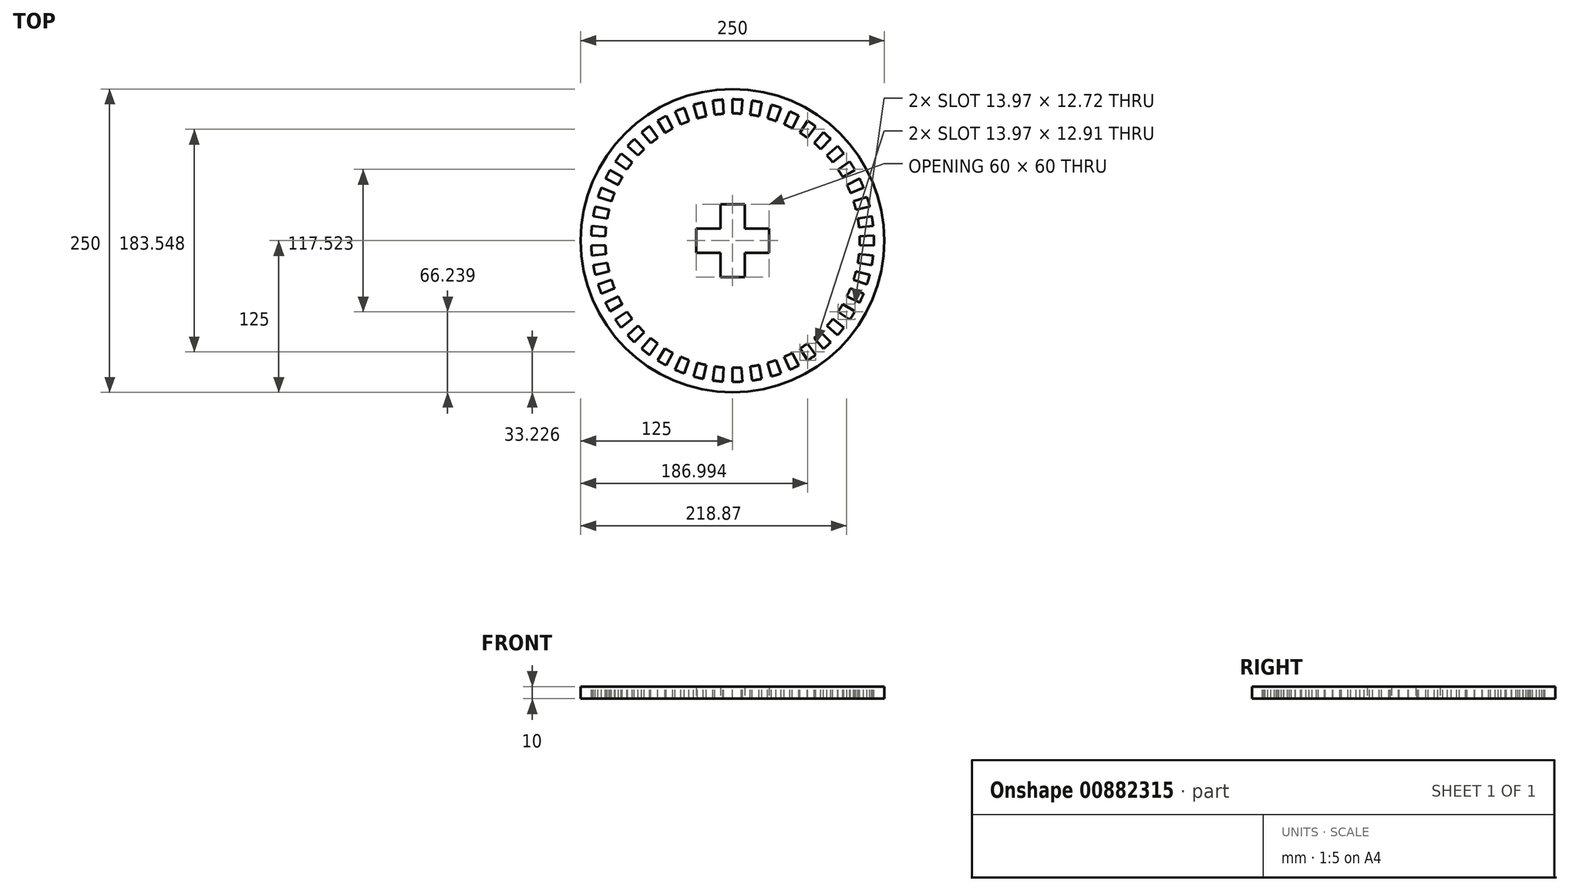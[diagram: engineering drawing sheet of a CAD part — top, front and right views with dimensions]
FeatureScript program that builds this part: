
annotation { "Feature Type Name" : "Feature", "Feature Type Description" : "" }
export const myFeature = defineFeature(function(context is Context, id is Id, definition is map)
    precondition{}
    {
        {
            var Q0;
            Q0=qCreatedBy(makeId("Top.planeOp"),FACE);
            var sketch = newSketch(context, id + "F0", { "sketchPlane" : qUnion([Q0])});
            skCircle(sketch, "E0", {"center": v(0, 0) * mm, "radius": 145 * mm});
            skArc(sketch, "E1", {"start": v(9.54, 136.41) * mm, "mid": v(4.77, 136.66) * mm, "end": v(0, 136.75) * mm});
            skArc(sketch, "E2", {"start": v(8, 114.55) * mm, "mid": v(4, 114.76) * mm, "end": v(0, 114.83) * mm});
            skLineSegment(sketch, "E3", {"start": v(0, 0) * mm, "end": v(0, 38.61) * mm, "construction": true});
            skLineSegment(sketch, "E4", {"start": v(0, 38.61) * mm, "end": v(0, 0) * mm, "construction": true});
            skLineSegment(sketch, "E5", {"start": v(0, 0) * mm, "end": v(-47.77, 0) * mm, "construction": true});
            skLineSegment(sketch, "E6", {"start": v(0, 30) * mm, "end": v(-10, 30) * mm});
            skLineSegment(sketch, "E7", {"start": v(-10, 30) * mm, "end": v(-10, 10) * mm});
            skLineSegment(sketch, "E8", {"start": v(-10, 10) * mm, "end": v(-30, 10) * mm});
            skLineSegment(sketch, "E9", {"start": v(-30, 10) * mm, "end": v(-30, 0) * mm});
            skLineSegment(sketch, "E10.MirrorCS", {"start": v(-30, -10) * mm, "end": v(-30, 0) * mm});
            skLineSegment(sketch, "E11.MirrorCS", {"start": v(-10, -10) * mm, "end": v(-30, -10) * mm});
            skLineSegment(sketch, "E12.MirrorCS", {"start": v(-10, -30) * mm, "end": v(-10, -10) * mm});
            skLineSegment(sketch, "E13.MirrorCS", {"start": v(0, -30) * mm, "end": v(-10, -30) * mm});
            skLineSegment(sketch, "E14.MirrorCS", {"start": v(0, 30) * mm, "end": v(10, 30) * mm});
            skLineSegment(sketch, "E15.MirrorCS", {"start": v(10, 30) * mm, "end": v(10, 10) * mm});
            skLineSegment(sketch, "E16.MirrorCS", {"start": v(10, 10) * mm, "end": v(30, 10) * mm});
            skLineSegment(sketch, "E17.MirrorCS", {"start": v(30, 10) * mm, "end": v(30, 0) * mm});
            skLineSegment(sketch, "E18.MirrorCS", {"start": v(30, -10) * mm, "end": v(30, 0) * mm});
            skLineSegment(sketch, "E19.MirrorCS", {"start": v(10, -10) * mm, "end": v(30, -10) * mm});
            skLineSegment(sketch, "E20.MirrorCS", {"start": v(0, -30) * mm, "end": v(10, -30) * mm});
            skLineSegment(sketch, "E21.MirrorCS", {"start": v(10, -30) * mm, "end": v(10, -10) * mm});
            skLineSegment(sketch, "E22", {"start": v(0, 114.83) * mm, "end": v(0, 136.75) * mm});
            skLineSegment(sketch, "E23", {"start": v(8, 114.55) * mm, "end": v(9.54, 136.41) * mm});
            skArc(sketch, "E24.1.0", {"start": v(-10, 114.4) * mm, "mid": v(-14, 113.98) * mm, "end": v(-17.96, 113.42) * mm});
            skLineSegment(sketch, "E24.1.1", {"start": v(-17.96, 113.42) * mm, "end": v(-21.4, 135.06) * mm});
            skArc(sketch, "E24.1.2", {"start": v(-11.92, 136.23) * mm, "mid": v(-16.67, 135.73) * mm, "end": v(-21.4, 135.06) * mm});
            skLineSegment(sketch, "E24.1.3", {"start": v(-10, 114.4) * mm, "end": v(-11.92, 136.23) * mm});
            skArc(sketch, "E24.2.0", {"start": v(-27.78, 111.42) * mm, "mid": v(-31.65, 110.39) * mm, "end": v(-35.49, 109.21) * mm});
            skLineSegment(sketch, "E24.2.1", {"start": v(-35.49, 109.21) * mm, "end": v(-42.26, 130.05) * mm});
            skArc(sketch, "E24.2.2", {"start": v(-33.08, 132.68) * mm, "mid": v(-37.7, 131.45) * mm, "end": v(-42.26, 130.05) * mm});
            skLineSegment(sketch, "E24.2.3", {"start": v(-27.78, 111.42) * mm, "end": v(-33.08, 132.68) * mm});
            skArc(sketch, "E24.3.0", {"start": v(-44.87, 105.7) * mm, "mid": v(-48.53, 104.07) * mm, "end": v(-52.13, 102.32) * mm});
            skLineSegment(sketch, "E24.3.1", {"start": v(-52.13, 102.32) * mm, "end": v(-62.08, 121.84) * mm});
            skArc(sketch, "E24.3.2", {"start": v(-53.43, 125.88) * mm, "mid": v(-57.8, 123.93) * mm, "end": v(-62.08, 121.84) * mm});
            skLineSegment(sketch, "E24.3.3", {"start": v(-44.87, 105.7) * mm, "end": v(-53.43, 125.88) * mm});
            skArc(sketch, "E24.4.0", {"start": v(-60.85, 97.38) * mm, "mid": v(-64.21, 95.2) * mm, "end": v(-67.5, 92.9) * mm});
            skLineSegment(sketch, "E24.4.1", {"start": v(-67.5, 92.9) * mm, "end": v(-80.38, 110.63) * mm});
            skArc(sketch, "E24.4.2", {"start": v(-72.47, 115.97) * mm, "mid": v(-76.47, 113.37) * mm, "end": v(-80.38, 110.63) * mm});
            skLineSegment(sketch, "E24.4.3", {"start": v(-60.85, 97.38) * mm, "end": v(-72.47, 115.97) * mm});
            skArc(sketch, "E24.5.0", {"start": v(-75.34, 86.67) * mm, "mid": v(-78.32, 83.98) * mm, "end": v(-81.2, 81.2) * mm});
            skLineSegment(sketch, "E24.5.1", {"start": v(-81.2, 81.2) * mm, "end": v(-96.7, 96.7) * mm});
            skArc(sketch, "E24.5.2", {"start": v(-89.71, 103.2) * mm, "mid": v(-93.26, 100.01) * mm, "end": v(-96.7, 96.7) * mm});
            skLineSegment(sketch, "E24.5.3", {"start": v(-75.34, 86.67) * mm, "end": v(-89.71, 103.2) * mm});
            skArc(sketch, "E24.6.0", {"start": v(-87.97, 73.81) * mm, "mid": v(-90.5, 70.7) * mm, "end": v(-92.9, 67.5) * mm});
            skLineSegment(sketch, "E24.6.1", {"start": v(-92.9, 67.5) * mm, "end": v(-110.63, 80.38) * mm});
            skArc(sketch, "E24.6.2", {"start": v(-104.75, 87.9) * mm, "mid": v(-107.76, 84.19) * mm, "end": v(-110.63, 80.38) * mm});
            skLineSegment(sketch, "E24.6.3", {"start": v(-87.97, 73.81) * mm, "end": v(-104.75, 87.9) * mm});
            skArc(sketch, "E24.7.0", {"start": v(-98.43, 59.14) * mm, "mid": v(-100.44, 55.67) * mm, "end": v(-102.32, 52.13) * mm});
            skLineSegment(sketch, "E24.7.1", {"start": v(-102.32, 52.13) * mm, "end": v(-121.84, 62.08) * mm});
            skArc(sketch, "E24.7.2", {"start": v(-117.22, 70.43) * mm, "mid": v(-119.6, 66.3) * mm, "end": v(-121.84, 62.08) * mm});
            skLineSegment(sketch, "E24.7.3", {"start": v(-98.43, 59.14) * mm, "end": v(-117.22, 70.43) * mm});
            skArc(sketch, "E24.8.0", {"start": v(-106.47, 43.02) * mm, "mid": v(-107.9, 39.28) * mm, "end": v(-109.21, 35.49) * mm});
            skLineSegment(sketch, "E24.8.1", {"start": v(-109.21, 35.49) * mm, "end": v(-130.05, 42.26) * mm});
            skArc(sketch, "E24.8.2", {"start": v(-126.79, 51.23) * mm, "mid": v(-128.5, 46.77) * mm, "end": v(-130.05, 42.26) * mm});
            skLineSegment(sketch, "E24.8.3", {"start": v(-106.47, 43.02) * mm, "end": v(-126.79, 51.23) * mm});
            skArc(sketch, "E24.9.0", {"start": v(-111.9, 25.83) * mm, "mid": v(-112.72, 21.91) * mm, "end": v(-113.42, 17.96) * mm});
            skLineSegment(sketch, "E24.9.1", {"start": v(-113.42, 17.96) * mm, "end": v(-135.06, 21.4) * mm});
            skArc(sketch, "E24.9.2", {"start": v(-133.24, 30.76) * mm, "mid": v(-134.23, 26.1) * mm, "end": v(-135.06, 21.4) * mm});
            skLineSegment(sketch, "E24.9.3", {"start": v(-111.9, 25.83) * mm, "end": v(-133.24, 30.76) * mm});
            skArc(sketch, "E24.10.0", {"start": v(-114.55, 8) * mm, "mid": v(-114.76, 4) * mm, "end": v(-114.83, 0) * mm});
            skLineSegment(sketch, "E24.10.1", {"start": v(-114.83, 0) * mm, "end": v(-136.75, 0) * mm});
            skArc(sketch, "E24.10.2", {"start": v(-136.41, 9.54) * mm, "mid": v(-136.66, 4.77) * mm, "end": v(-136.75, 0) * mm});
            skLineSegment(sketch, "E24.10.3", {"start": v(-114.55, 8) * mm, "end": v(-136.41, 9.54) * mm});
            skArc(sketch, "E24.11.0", {"start": v(-114.4, -10) * mm, "mid": v(-113.98, -14) * mm, "end": v(-113.42, -17.96) * mm});
            skLineSegment(sketch, "E24.11.1", {"start": v(-113.42, -17.96) * mm, "end": v(-135.06, -21.4) * mm});
            skArc(sketch, "E24.11.2", {"start": v(-136.23, -11.92) * mm, "mid": v(-135.73, -16.67) * mm, "end": v(-135.06, -21.4) * mm});
            skLineSegment(sketch, "E24.11.3", {"start": v(-114.4, -10) * mm, "end": v(-136.23, -11.92) * mm});
            skArc(sketch, "E24.12.0", {"start": v(-111.42, -27.78) * mm, "mid": v(-110.39, -31.65) * mm, "end": v(-109.21, -35.49) * mm});
            skLineSegment(sketch, "E24.12.1", {"start": v(-109.21, -35.49) * mm, "end": v(-130.05, -42.26) * mm});
            skArc(sketch, "E24.12.2", {"start": v(-132.68, -33.08) * mm, "mid": v(-131.45, -37.7) * mm, "end": v(-130.05, -42.26) * mm});
            skLineSegment(sketch, "E24.12.3", {"start": v(-111.42, -27.78) * mm, "end": v(-132.68, -33.08) * mm});
            skArc(sketch, "E24.13.0", {"start": v(-105.7, -44.87) * mm, "mid": v(-104.07, -48.53) * mm, "end": v(-102.32, -52.13) * mm});
            skLineSegment(sketch, "E24.13.1", {"start": v(-102.32, -52.13) * mm, "end": v(-121.84, -62.08) * mm});
            skArc(sketch, "E24.13.2", {"start": v(-125.88, -53.43) * mm, "mid": v(-123.93, -57.8) * mm, "end": v(-121.84, -62.08) * mm});
            skLineSegment(sketch, "E24.13.3", {"start": v(-105.7, -44.87) * mm, "end": v(-125.88, -53.43) * mm});
            skArc(sketch, "E24.14.0", {"start": v(-97.38, -60.85) * mm, "mid": v(-95.2, -64.21) * mm, "end": v(-92.9, -67.5) * mm});
            skLineSegment(sketch, "E24.14.1", {"start": v(-92.9, -67.5) * mm, "end": v(-110.63, -80.38) * mm});
            skArc(sketch, "E24.14.2", {"start": v(-115.97, -72.47) * mm, "mid": v(-113.37, -76.47) * mm, "end": v(-110.63, -80.38) * mm});
            skLineSegment(sketch, "E24.14.3", {"start": v(-97.38, -60.85) * mm, "end": v(-115.97, -72.47) * mm});
            skArc(sketch, "E24.15.0", {"start": v(-86.67, -75.34) * mm, "mid": v(-83.98, -78.32) * mm, "end": v(-81.2, -81.2) * mm});
            skLineSegment(sketch, "E24.15.1", {"start": v(-81.2, -81.2) * mm, "end": v(-96.7, -96.7) * mm});
            skArc(sketch, "E24.15.2", {"start": v(-103.2, -89.71) * mm, "mid": v(-100.01, -93.26) * mm, "end": v(-96.7, -96.7) * mm});
            skLineSegment(sketch, "E24.15.3", {"start": v(-86.67, -75.34) * mm, "end": v(-103.2, -89.71) * mm});
            skArc(sketch, "E24.16.0", {"start": v(-73.81, -87.97) * mm, "mid": v(-70.7, -90.5) * mm, "end": v(-67.5, -92.9) * mm});
            skLineSegment(sketch, "E24.16.1", {"start": v(-67.5, -92.9) * mm, "end": v(-80.38, -110.63) * mm});
            skArc(sketch, "E24.16.2", {"start": v(-87.9, -104.75) * mm, "mid": v(-84.19, -107.76) * mm, "end": v(-80.38, -110.63) * mm});
            skLineSegment(sketch, "E24.16.3", {"start": v(-73.81, -87.97) * mm, "end": v(-87.9, -104.75) * mm});
            skArc(sketch, "E24.17.0", {"start": v(-59.14, -98.43) * mm, "mid": v(-55.67, -100.44) * mm, "end": v(-52.13, -102.32) * mm});
            skLineSegment(sketch, "E24.17.1", {"start": v(-52.13, -102.32) * mm, "end": v(-62.08, -121.84) * mm});
            skArc(sketch, "E24.17.2", {"start": v(-70.43, -117.22) * mm, "mid": v(-66.3, -119.6) * mm, "end": v(-62.08, -121.84) * mm});
            skLineSegment(sketch, "E24.17.3", {"start": v(-59.14, -98.43) * mm, "end": v(-70.43, -117.22) * mm});
            skArc(sketch, "E24.18.0", {"start": v(-43.02, -106.47) * mm, "mid": v(-39.28, -107.9) * mm, "end": v(-35.49, -109.21) * mm});
            skLineSegment(sketch, "E24.18.1", {"start": v(-35.49, -109.21) * mm, "end": v(-42.26, -130.05) * mm});
            skArc(sketch, "E24.18.2", {"start": v(-51.23, -126.79) * mm, "mid": v(-46.77, -128.5) * mm, "end": v(-42.26, -130.05) * mm});
            skLineSegment(sketch, "E24.18.3", {"start": v(-43.02, -106.47) * mm, "end": v(-51.23, -126.79) * mm});
            skArc(sketch, "E24.19.0", {"start": v(-25.83, -111.9) * mm, "mid": v(-21.91, -112.72) * mm, "end": v(-17.96, -113.42) * mm});
            skLineSegment(sketch, "E24.19.1", {"start": v(-17.96, -113.42) * mm, "end": v(-21.4, -135.06) * mm});
            skArc(sketch, "E24.19.2", {"start": v(-30.76, -133.24) * mm, "mid": v(-26.1, -134.23) * mm, "end": v(-21.4, -135.06) * mm});
            skLineSegment(sketch, "E24.19.3", {"start": v(-25.83, -111.9) * mm, "end": v(-30.76, -133.24) * mm});
            skArc(sketch, "E24.20.0", {"start": v(-8, -114.55) * mm, "mid": v(-4, -114.76) * mm, "end": v(0, -114.83) * mm});
            skLineSegment(sketch, "E24.20.1", {"start": v(0, -114.83) * mm, "end": v(0, -136.75) * mm});
            skArc(sketch, "E24.20.2", {"start": v(-9.54, -136.41) * mm, "mid": v(-4.77, -136.66) * mm, "end": v(0, -136.75) * mm});
            skLineSegment(sketch, "E24.20.3", {"start": v(-8, -114.55) * mm, "end": v(-9.54, -136.41) * mm});
            skArc(sketch, "E24.21.0", {"start": v(10, -114.4) * mm, "mid": v(14, -113.98) * mm, "end": v(17.96, -113.42) * mm});
            skLineSegment(sketch, "E24.21.1", {"start": v(17.96, -113.42) * mm, "end": v(21.4, -135.06) * mm});
            skArc(sketch, "E24.21.2", {"start": v(11.92, -136.23) * mm, "mid": v(16.67, -135.73) * mm, "end": v(21.4, -135.06) * mm});
            skLineSegment(sketch, "E24.21.3", {"start": v(10, -114.4) * mm, "end": v(11.92, -136.23) * mm});
            skArc(sketch, "E24.22.0", {"start": v(27.78, -111.42) * mm, "mid": v(31.65, -110.39) * mm, "end": v(35.49, -109.21) * mm});
            skLineSegment(sketch, "E24.22.1", {"start": v(35.49, -109.21) * mm, "end": v(42.26, -130.05) * mm});
            skArc(sketch, "E24.22.2", {"start": v(33.08, -132.68) * mm, "mid": v(37.7, -131.45) * mm, "end": v(42.26, -130.05) * mm});
            skLineSegment(sketch, "E24.22.3", {"start": v(27.78, -111.42) * mm, "end": v(33.08, -132.68) * mm});
            skArc(sketch, "E24.23.0", {"start": v(44.87, -105.7) * mm, "mid": v(48.53, -104.07) * mm, "end": v(52.13, -102.32) * mm});
            skLineSegment(sketch, "E24.23.1", {"start": v(52.13, -102.32) * mm, "end": v(62.08, -121.84) * mm});
            skArc(sketch, "E24.23.2", {"start": v(53.43, -125.88) * mm, "mid": v(57.8, -123.93) * mm, "end": v(62.08, -121.84) * mm});
            skLineSegment(sketch, "E24.23.3", {"start": v(44.87, -105.7) * mm, "end": v(53.43, -125.88) * mm});
            skArc(sketch, "E24.24.0", {"start": v(60.85, -97.38) * mm, "mid": v(64.21, -95.2) * mm, "end": v(67.5, -92.9) * mm});
            skLineSegment(sketch, "E24.24.1", {"start": v(67.5, -92.9) * mm, "end": v(80.38, -110.63) * mm});
            skArc(sketch, "E24.24.2", {"start": v(72.47, -115.97) * mm, "mid": v(76.47, -113.37) * mm, "end": v(80.38, -110.63) * mm});
            skLineSegment(sketch, "E24.24.3", {"start": v(60.85, -97.38) * mm, "end": v(72.47, -115.97) * mm});
            skArc(sketch, "E24.25.0", {"start": v(75.34, -86.67) * mm, "mid": v(78.32, -83.98) * mm, "end": v(81.2, -81.2) * mm});
            skLineSegment(sketch, "E24.25.1", {"start": v(81.2, -81.2) * mm, "end": v(96.7, -96.7) * mm});
            skArc(sketch, "E24.25.2", {"start": v(89.71, -103.2) * mm, "mid": v(93.26, -100.01) * mm, "end": v(96.7, -96.7) * mm});
            skLineSegment(sketch, "E24.25.3", {"start": v(75.34, -86.67) * mm, "end": v(89.71, -103.2) * mm});
            skArc(sketch, "E24.26.0", {"start": v(87.97, -73.81) * mm, "mid": v(90.5, -70.7) * mm, "end": v(92.9, -67.5) * mm});
            skLineSegment(sketch, "E24.26.1", {"start": v(92.9, -67.5) * mm, "end": v(110.63, -80.38) * mm});
            skArc(sketch, "E24.26.2", {"start": v(104.75, -87.9) * mm, "mid": v(107.76, -84.19) * mm, "end": v(110.63, -80.38) * mm});
            skLineSegment(sketch, "E24.26.3", {"start": v(87.97, -73.81) * mm, "end": v(104.75, -87.9) * mm});
            skArc(sketch, "E24.27.0", {"start": v(98.43, -59.14) * mm, "mid": v(100.44, -55.67) * mm, "end": v(102.32, -52.13) * mm});
            skLineSegment(sketch, "E24.27.1", {"start": v(102.32, -52.13) * mm, "end": v(121.84, -62.08) * mm});
            skArc(sketch, "E24.27.2", {"start": v(117.22, -70.43) * mm, "mid": v(119.6, -66.3) * mm, "end": v(121.84, -62.08) * mm});
            skLineSegment(sketch, "E24.27.3", {"start": v(98.43, -59.14) * mm, "end": v(117.22, -70.43) * mm});
            skArc(sketch, "E24.28.0", {"start": v(106.47, -43.02) * mm, "mid": v(107.9, -39.28) * mm, "end": v(109.21, -35.49) * mm});
            skLineSegment(sketch, "E24.28.1", {"start": v(109.21, -35.49) * mm, "end": v(130.05, -42.26) * mm});
            skArc(sketch, "E24.28.2", {"start": v(126.79, -51.23) * mm, "mid": v(128.5, -46.77) * mm, "end": v(130.05, -42.26) * mm});
            skLineSegment(sketch, "E24.28.3", {"start": v(106.47, -43.02) * mm, "end": v(126.79, -51.23) * mm});
            skArc(sketch, "E24.29.0", {"start": v(111.9, -25.83) * mm, "mid": v(112.72, -21.91) * mm, "end": v(113.42, -17.96) * mm});
            skLineSegment(sketch, "E24.29.1", {"start": v(113.42, -17.96) * mm, "end": v(135.06, -21.4) * mm});
            skArc(sketch, "E24.29.2", {"start": v(133.24, -30.76) * mm, "mid": v(134.23, -26.1) * mm, "end": v(135.06, -21.4) * mm});
            skLineSegment(sketch, "E24.29.3", {"start": v(111.9, -25.83) * mm, "end": v(133.24, -30.76) * mm});
            skArc(sketch, "E24.30.0", {"start": v(114.55, -8) * mm, "mid": v(114.76, -4) * mm, "end": v(114.83, 0) * mm});
            skLineSegment(sketch, "E24.30.1", {"start": v(114.83, 0) * mm, "end": v(136.75, 0) * mm});
            skArc(sketch, "E24.30.2", {"start": v(136.41, -9.54) * mm, "mid": v(136.66, -4.77) * mm, "end": v(136.75, 0) * mm});
            skLineSegment(sketch, "E24.30.3", {"start": v(114.55, -8) * mm, "end": v(136.41, -9.54) * mm});
            skArc(sketch, "E24.31.0", {"start": v(114.4, 10) * mm, "mid": v(113.98, 14) * mm, "end": v(113.42, 17.96) * mm});
            skLineSegment(sketch, "E24.31.1", {"start": v(113.42, 17.96) * mm, "end": v(135.06, 21.4) * mm});
            skArc(sketch, "E24.31.2", {"start": v(136.23, 11.92) * mm, "mid": v(135.73, 16.67) * mm, "end": v(135.06, 21.4) * mm});
            skLineSegment(sketch, "E24.31.3", {"start": v(114.4, 10) * mm, "end": v(136.23, 11.92) * mm});
            skArc(sketch, "E24.32.0", {"start": v(111.42, 27.78) * mm, "mid": v(110.39, 31.65) * mm, "end": v(109.21, 35.49) * mm});
            skLineSegment(sketch, "E24.32.1", {"start": v(109.21, 35.49) * mm, "end": v(130.05, 42.26) * mm});
            skArc(sketch, "E24.32.2", {"start": v(132.68, 33.08) * mm, "mid": v(131.45, 37.7) * mm, "end": v(130.05, 42.26) * mm});
            skLineSegment(sketch, "E24.32.3", {"start": v(111.42, 27.78) * mm, "end": v(132.68, 33.08) * mm});
            skArc(sketch, "E24.33.0", {"start": v(105.7, 44.87) * mm, "mid": v(104.07, 48.53) * mm, "end": v(102.32, 52.13) * mm});
            skLineSegment(sketch, "E24.33.1", {"start": v(102.32, 52.13) * mm, "end": v(121.84, 62.08) * mm});
            skArc(sketch, "E24.33.2", {"start": v(125.88, 53.43) * mm, "mid": v(123.93, 57.8) * mm, "end": v(121.84, 62.08) * mm});
            skLineSegment(sketch, "E24.33.3", {"start": v(105.7, 44.87) * mm, "end": v(125.88, 53.43) * mm});
            skArc(sketch, "E24.34.0", {"start": v(97.38, 60.85) * mm, "mid": v(95.2, 64.21) * mm, "end": v(92.9, 67.5) * mm});
            skLineSegment(sketch, "E24.34.1", {"start": v(92.9, 67.5) * mm, "end": v(110.63, 80.38) * mm});
            skArc(sketch, "E24.34.2", {"start": v(115.97, 72.47) * mm, "mid": v(113.37, 76.47) * mm, "end": v(110.63, 80.38) * mm});
            skLineSegment(sketch, "E24.34.3", {"start": v(97.38, 60.85) * mm, "end": v(115.97, 72.47) * mm});
            skArc(sketch, "E24.35.0", {"start": v(86.67, 75.34) * mm, "mid": v(83.98, 78.32) * mm, "end": v(81.2, 81.2) * mm});
            skLineSegment(sketch, "E24.35.1", {"start": v(81.2, 81.2) * mm, "end": v(96.7, 96.7) * mm});
            skArc(sketch, "E24.35.2", {"start": v(103.2, 89.71) * mm, "mid": v(100.01, 93.26) * mm, "end": v(96.7, 96.7) * mm});
            skLineSegment(sketch, "E24.35.3", {"start": v(86.67, 75.34) * mm, "end": v(103.2, 89.71) * mm});
            skArc(sketch, "E24.36.0", {"start": v(73.81, 87.97) * mm, "mid": v(70.7, 90.5) * mm, "end": v(67.5, 92.9) * mm});
            skLineSegment(sketch, "E24.36.1", {"start": v(67.5, 92.9) * mm, "end": v(80.38, 110.63) * mm});
            skArc(sketch, "E24.36.2", {"start": v(87.9, 104.75) * mm, "mid": v(84.19, 107.76) * mm, "end": v(80.38, 110.63) * mm});
            skLineSegment(sketch, "E24.36.3", {"start": v(73.81, 87.97) * mm, "end": v(87.9, 104.75) * mm});
            skArc(sketch, "E24.37.0", {"start": v(59.14, 98.43) * mm, "mid": v(55.67, 100.44) * mm, "end": v(52.13, 102.32) * mm});
            skLineSegment(sketch, "E24.37.1", {"start": v(52.13, 102.32) * mm, "end": v(62.08, 121.84) * mm});
            skArc(sketch, "E24.37.2", {"start": v(70.43, 117.22) * mm, "mid": v(66.3, 119.6) * mm, "end": v(62.08, 121.84) * mm});
            skLineSegment(sketch, "E24.37.3", {"start": v(59.14, 98.43) * mm, "end": v(70.43, 117.22) * mm});
            skArc(sketch, "E24.38.0", {"start": v(43.02, 106.47) * mm, "mid": v(39.28, 107.9) * mm, "end": v(35.49, 109.21) * mm});
            skLineSegment(sketch, "E24.38.1", {"start": v(35.49, 109.21) * mm, "end": v(42.26, 130.05) * mm});
            skArc(sketch, "E24.38.2", {"start": v(51.23, 126.79) * mm, "mid": v(46.77, 128.5) * mm, "end": v(42.26, 130.05) * mm});
            skLineSegment(sketch, "E24.38.3", {"start": v(43.02, 106.47) * mm, "end": v(51.23, 126.79) * mm});
            skArc(sketch, "E24.39.0", {"start": v(25.83, 111.9) * mm, "mid": v(21.91, 112.72) * mm, "end": v(17.96, 113.42) * mm});
            skLineSegment(sketch, "E24.39.1", {"start": v(17.96, 113.42) * mm, "end": v(21.4, 135.06) * mm});
            skArc(sketch, "E24.39.2", {"start": v(30.76, 133.24) * mm, "mid": v(26.1, 134.23) * mm, "end": v(21.4, 135.06) * mm});
            skLineSegment(sketch, "E24.39.3", {"start": v(25.83, 111.9) * mm, "end": v(30.76, 133.24) * mm});
            skCircle(sketch, "E25", {"center": v(0, 0) * mm, "radius": 50 * mm});
            skSolve(sketch);
        }
        {
            var Q0;
            Q0=makeQuery(id+"F0.imprint","IMPRINT",FACE,{"disambiguationData":[TD([[makeQuery(id+"F0.imprint","IMPRINT",EDGE,{"derivedFrom":sQuery(id+"F0.wireOp",EDGE,"E6")}),-1.0]])]});
            extrude(context, id + "F1", {"entities" : qUnion([Q0]), "depth" : 10 * mm, "offsetDistance" : 25 * mm});
        }
        {
            var Q0;
            Q0=makeQuery(id+"F1.opExtrude","CAP_FACE",FACE,{"disambiguationData":[OSD([sQuery(id+"F0.wireOp",EDGE,"E6"),sQuery(id+"F0.wireOp",EDGE,"E7"),sQuery(id+"F0.wireOp",EDGE,"E8"),sQuery(id+"F0.wireOp",EDGE,"E9"),sQuery(id+"F0.wireOp",EDGE,"E10.MirrorCS"),sQuery(id+"F0.wireOp",EDGE,"E11.MirrorCS"),sQuery(id+"F0.wireOp",EDGE,"E12.MirrorCS"),sQuery(id+"F0.wireOp",EDGE,"E13.MirrorCS"),sQuery(id+"F0.wireOp",EDGE,"E14.MirrorCS"),sQuery(id+"F0.wireOp",EDGE,"E15.MirrorCS"),sQuery(id+"F0.wireOp",EDGE,"E16.MirrorCS"),sQuery(id+"F0.wireOp",EDGE,"E17.MirrorCS"),sQuery(id+"F0.wireOp",EDGE,"E18.MirrorCS"),sQuery(id+"F0.wireOp",EDGE,"E19.MirrorCS"),sQuery(id+"F0.wireOp",EDGE,"E20.MirrorCS"),sQuery(id+"F0.wireOp",EDGE,"E21.MirrorCS"),sQuery(id+"F0.wireOp",EDGE,"E25")])],"isStart":false});
            var sketch = newSketch(context, id + "F2", { "sketchPlane" : qUnion([Q0])});
            skCircle(sketch, "E26", {"center": v(0, 0) * mm, "radius": 125 * mm});
            skCircle(sketch, "E27", {"center": v(0, 0) * mm, "radius": 40.45 * mm});
            skSolve(sketch);
        }
        {
            var Q0;
            Q0 = qSketchRegion(id + "F2", true);
            extrude(context, id + "F3", {"entities" : qUnion([Q0]), "operationType" : NewBodyOperationType.ADD, "oppositeDirection" : true, "depth" : 10 * mm, "offsetDistance" : 25 * mm});
        }
        {
            var Q0;
            Q0=makeQuery(id+"F3.boolean.opBoolean","MERGE",FACE,{"derivedFrom":[makeQuery(id+"F1.opExtrude","CAP_FACE",FACE,{"disambiguationData":[OSD([sQuery(id+"F0.wireOp",EDGE,"E6"),sQuery(id+"F0.wireOp",EDGE,"E7"),sQuery(id+"F0.wireOp",EDGE,"E8"),sQuery(id+"F0.wireOp",EDGE,"E9"),sQuery(id+"F0.wireOp",EDGE,"E10.MirrorCS"),sQuery(id+"F0.wireOp",EDGE,"E11.MirrorCS"),sQuery(id+"F0.wireOp",EDGE,"E12.MirrorCS"),sQuery(id+"F0.wireOp",EDGE,"E13.MirrorCS"),sQuery(id+"F0.wireOp",EDGE,"E14.MirrorCS"),sQuery(id+"F0.wireOp",EDGE,"E15.MirrorCS"),sQuery(id+"F0.wireOp",EDGE,"E16.MirrorCS"),sQuery(id+"F0.wireOp",EDGE,"E17.MirrorCS"),sQuery(id+"F0.wireOp",EDGE,"E18.MirrorCS"),sQuery(id+"F0.wireOp",EDGE,"E19.MirrorCS"),sQuery(id+"F0.wireOp",EDGE,"E20.MirrorCS"),sQuery(id+"F0.wireOp",EDGE,"E21.MirrorCS"),sQuery(id+"F0.wireOp",EDGE,"E25")])],"isStart":false}),makeQuery(id+"F3.opExtrude","CAP_FACE",FACE,{"disambiguationData":[OSD([sQuery(id+"F2.wireOp",EDGE,"E26"),sQuery(id+"F2.wireOp",EDGE,"E27")])],"isStart":true})]});
            var sketch = newSketch(context, id + "F4", { "sketchPlane" : qUnion([Q0])});
            skLineSegment(sketch, "E28", {"start": v(0, 104.8) * mm, "end": v(0, 116.46) * mm});
            skLineSegment(sketch, "E29", {"start": v(0, 116.46) * mm, "end": v(0, 104.8) * mm});
            skLineSegment(sketch, "E30", {"start": v(7.31, 104.55) * mm, "end": v(8.12, 116.17) * mm});
            skArc(sketch, "E31", {"start": v(8.12, 116.17) * mm, "mid": v(4.06, 116.39) * mm, "end": v(0, 116.46) * mm});
            skArc(sketch, "E32", {"start": v(7.31, 104.55) * mm, "mid": v(3.66, 104.74) * mm, "end": v(0, 104.8) * mm});
            skArc(sketch, "E33.1.0", {"start": v(-7.31, 104.55) * mm, "mid": v(-10.95, 104.23) * mm, "end": v(-14.59, 103.78) * mm});
            skLineSegment(sketch, "E33.1.1", {"start": v(-16.2, 115.32) * mm, "end": v(-14.59, 103.78) * mm});
            skArc(sketch, "E33.1.2", {"start": v(-8.12, 116.17) * mm, "mid": v(-12.17, 115.82) * mm, "end": v(-16.2, 115.32) * mm});
            skLineSegment(sketch, "E33.1.3", {"start": v(-7.31, 104.55) * mm, "end": v(-8.12, 116.17) * mm});
            skArc(sketch, "E33.2.0", {"start": v(-21.79, 102.51) * mm, "mid": v(-25.35, 101.69) * mm, "end": v(-28.89, 100.74) * mm});
            skLineSegment(sketch, "E33.2.1", {"start": v(-32.1, 111.95) * mm, "end": v(-28.89, 100.74) * mm});
            skArc(sketch, "E33.2.2", {"start": v(-24.21, 113.91) * mm, "mid": v(-28.17, 113) * mm, "end": v(-32.1, 111.95) * mm});
            skLineSegment(sketch, "E33.2.3", {"start": v(-21.79, 102.51) * mm, "end": v(-24.21, 113.91) * mm});
            skArc(sketch, "E33.3.0", {"start": v(-35.84, 98.48) * mm, "mid": v(-39.26, 97.17) * mm, "end": v(-42.63, 95.74) * mm});
            skLineSegment(sketch, "E33.3.1", {"start": v(-47.37, 106.39) * mm, "end": v(-42.63, 95.74) * mm});
            skArc(sketch, "E33.3.2", {"start": v(-39.83, 109.43) * mm, "mid": v(-43.63, 107.98) * mm, "end": v(-47.37, 106.39) * mm});
            skLineSegment(sketch, "E33.3.3", {"start": v(-35.84, 98.48) * mm, "end": v(-39.83, 109.43) * mm});
            skArc(sketch, "E33.4.0", {"start": v(-49.2, 92.54) * mm, "mid": v(-52.4, 90.76) * mm, "end": v(-55.54, 88.88) * mm});
            skLineSegment(sketch, "E33.4.1", {"start": v(-61.71, 98.76) * mm, "end": v(-55.54, 88.88) * mm});
            skArc(sketch, "E33.4.2", {"start": v(-54.67, 102.82) * mm, "mid": v(-58.23, 100.85) * mm, "end": v(-61.71, 98.76) * mm});
            skLineSegment(sketch, "E33.4.3", {"start": v(-49.2, 92.54) * mm, "end": v(-54.67, 102.82) * mm});
            skArc(sketch, "E33.5.0", {"start": v(-61.6, 84.79) * mm, "mid": v(-64.52, 82.59) * mm, "end": v(-67.37, 80.28) * mm});
            skLineSegment(sketch, "E33.5.1", {"start": v(-74.86, 89.21) * mm, "end": v(-67.37, 80.28) * mm});
            skArc(sketch, "E33.5.2", {"start": v(-68.45, 94.22) * mm, "mid": v(-71.7, 91.77) * mm, "end": v(-74.86, 89.21) * mm});
            skLineSegment(sketch, "E33.5.3", {"start": v(-61.6, 84.79) * mm, "end": v(-68.45, 94.22) * mm});
            skArc(sketch, "E33.6.0", {"start": v(-72.8, 75.39) * mm, "mid": v(-75.39, 72.8) * mm, "end": v(-77.88, 70.13) * mm});
            skLineSegment(sketch, "E33.6.1", {"start": v(-86.54, 77.92) * mm, "end": v(-77.88, 70.13) * mm});
            skArc(sketch, "E33.6.2", {"start": v(-80.9, 83.77) * mm, "mid": v(-83.77, 80.9) * mm, "end": v(-86.54, 77.92) * mm});
            skLineSegment(sketch, "E33.6.3", {"start": v(-72.8, 75.39) * mm, "end": v(-80.9, 83.77) * mm});
            skArc(sketch, "E33.7.0", {"start": v(-82.59, 64.52) * mm, "mid": v(-84.79, 61.6) * mm, "end": v(-86.89, 58.6) * mm});
            skLineSegment(sketch, "E33.7.1", {"start": v(-96.55, 65.12) * mm, "end": v(-86.89, 58.6) * mm});
            skArc(sketch, "E33.7.2", {"start": v(-91.77, 71.7) * mm, "mid": v(-94.22, 68.45) * mm, "end": v(-96.55, 65.12) * mm});
            skLineSegment(sketch, "E33.7.3", {"start": v(-82.59, 64.52) * mm, "end": v(-91.77, 71.7) * mm});
            skArc(sketch, "E33.8.0", {"start": v(-90.76, 52.4) * mm, "mid": v(-92.54, 49.2) * mm, "end": v(-94.2, 45.94) * mm});
            skLineSegment(sketch, "E33.8.1", {"start": v(-104.67, 51.05) * mm, "end": v(-94.2, 45.94) * mm});
            skArc(sketch, "E33.8.2", {"start": v(-100.85, 58.23) * mm, "mid": v(-102.82, 54.67) * mm, "end": v(-104.67, 51.05) * mm});
            skLineSegment(sketch, "E33.8.3", {"start": v(-90.76, 52.4) * mm, "end": v(-100.85, 58.23) * mm});
            skArc(sketch, "E33.9.0", {"start": v(-97.17, 39.26) * mm, "mid": v(-98.48, 35.84) * mm, "end": v(-99.67, 32.39) * mm});
            skLineSegment(sketch, "E33.9.1", {"start": v(-110.76, 35.99) * mm, "end": v(-99.67, 32.39) * mm});
            skArc(sketch, "E33.9.2", {"start": v(-107.98, 43.63) * mm, "mid": v(-109.43, 39.83) * mm, "end": v(-110.76, 35.99) * mm});
            skLineSegment(sketch, "E33.9.3", {"start": v(-97.17, 39.26) * mm, "end": v(-107.98, 43.63) * mm});
            skArc(sketch, "E33.10.0", {"start": v(-101.69, 25.35) * mm, "mid": v(-102.51, 21.79) * mm, "end": v(-103.21, 18.2) * mm});
            skLineSegment(sketch, "E33.10.1", {"start": v(-114.69, 20.22) * mm, "end": v(-103.21, 18.2) * mm});
            skArc(sketch, "E33.10.2", {"start": v(-113, 28.17) * mm, "mid": v(-113.91, 24.21) * mm, "end": v(-114.69, 20.22) * mm});
            skLineSegment(sketch, "E33.10.3", {"start": v(-101.69, 25.35) * mm, "end": v(-113, 28.17) * mm});
            skArc(sketch, "E33.11.0", {"start": v(-104.23, 10.95) * mm, "mid": v(-104.55, 7.31) * mm, "end": v(-104.74, 3.66) * mm});
            skLineSegment(sketch, "E33.11.1", {"start": v(-116.39, 4.06) * mm, "end": v(-104.74, 3.66) * mm});
            skArc(sketch, "E33.11.2", {"start": v(-115.82, 12.17) * mm, "mid": v(-116.17, 8.12) * mm, "end": v(-116.39, 4.06) * mm});
            skLineSegment(sketch, "E33.11.3", {"start": v(-104.23, 10.95) * mm, "end": v(-115.82, 12.17) * mm});
            skArc(sketch, "E33.12.0", {"start": v(-104.74, -3.66) * mm, "mid": v(-104.55, -7.31) * mm, "end": v(-104.23, -10.95) * mm});
            skLineSegment(sketch, "E33.12.1", {"start": v(-115.82, -12.17) * mm, "end": v(-104.23, -10.95) * mm});
            skArc(sketch, "E33.12.2", {"start": v(-116.39, -4.06) * mm, "mid": v(-116.17, -8.12) * mm, "end": v(-115.82, -12.17) * mm});
            skLineSegment(sketch, "E33.12.3", {"start": v(-104.74, -3.66) * mm, "end": v(-116.39, -4.06) * mm});
            skArc(sketch, "E33.13.0", {"start": v(-103.21, -18.2) * mm, "mid": v(-102.51, -21.79) * mm, "end": v(-101.69, -25.35) * mm});
            skLineSegment(sketch, "E33.13.1", {"start": v(-113, -28.17) * mm, "end": v(-101.69, -25.35) * mm});
            skArc(sketch, "E33.13.2", {"start": v(-114.69, -20.22) * mm, "mid": v(-113.91, -24.21) * mm, "end": v(-113, -28.17) * mm});
            skLineSegment(sketch, "E33.13.3", {"start": v(-103.21, -18.2) * mm, "end": v(-114.69, -20.22) * mm});
            skArc(sketch, "E33.14.0", {"start": v(-99.67, -32.39) * mm, "mid": v(-98.48, -35.84) * mm, "end": v(-97.17, -39.26) * mm});
            skLineSegment(sketch, "E33.14.1", {"start": v(-107.98, -43.63) * mm, "end": v(-97.17, -39.26) * mm});
            skArc(sketch, "E33.14.2", {"start": v(-110.76, -35.99) * mm, "mid": v(-109.43, -39.83) * mm, "end": v(-107.98, -43.63) * mm});
            skLineSegment(sketch, "E33.14.3", {"start": v(-99.67, -32.39) * mm, "end": v(-110.76, -35.99) * mm});
            skArc(sketch, "E33.15.0", {"start": v(-94.2, -45.94) * mm, "mid": v(-92.54, -49.2) * mm, "end": v(-90.76, -52.4) * mm});
            skLineSegment(sketch, "E33.15.1", {"start": v(-100.85, -58.23) * mm, "end": v(-90.76, -52.4) * mm});
            skArc(sketch, "E33.15.2", {"start": v(-104.67, -51.05) * mm, "mid": v(-102.82, -54.67) * mm, "end": v(-100.85, -58.23) * mm});
            skLineSegment(sketch, "E33.15.3", {"start": v(-94.2, -45.94) * mm, "end": v(-104.67, -51.05) * mm});
            skArc(sketch, "E33.16.0", {"start": v(-86.89, -58.6) * mm, "mid": v(-84.79, -61.6) * mm, "end": v(-82.59, -64.52) * mm});
            skLineSegment(sketch, "E33.16.1", {"start": v(-91.77, -71.7) * mm, "end": v(-82.59, -64.52) * mm});
            skArc(sketch, "E33.16.2", {"start": v(-96.55, -65.12) * mm, "mid": v(-94.22, -68.45) * mm, "end": v(-91.77, -71.7) * mm});
            skLineSegment(sketch, "E33.16.3", {"start": v(-86.89, -58.6) * mm, "end": v(-96.55, -65.12) * mm});
            skArc(sketch, "E33.17.0", {"start": v(-77.88, -70.13) * mm, "mid": v(-75.39, -72.8) * mm, "end": v(-72.8, -75.39) * mm});
            skLineSegment(sketch, "E33.17.1", {"start": v(-80.9, -83.77) * mm, "end": v(-72.8, -75.39) * mm});
            skArc(sketch, "E33.17.2", {"start": v(-86.54, -77.92) * mm, "mid": v(-83.77, -80.9) * mm, "end": v(-80.9, -83.77) * mm});
            skLineSegment(sketch, "E33.17.3", {"start": v(-77.88, -70.13) * mm, "end": v(-86.54, -77.92) * mm});
            skArc(sketch, "E34.3.18.0", {"start": v(-67.37, -80.28) * mm, "mid": v(-64.52, -82.59) * mm, "end": v(-61.6, -84.79) * mm});
            skLineSegment(sketch, "E34.4.18.0", {"start": v(-68.45, -94.22) * mm, "end": v(-61.6, -84.79) * mm});
            skArc(sketch, "E34.7.18.0", {"start": v(-74.86, -89.21) * mm, "mid": v(-71.7, -91.77) * mm, "end": v(-68.45, -94.22) * mm});
            skLineSegment(sketch, "E34.11.18.0", {"start": v(-67.37, -80.28) * mm, "end": v(-74.86, -89.21) * mm});
            skArc(sketch, "E34.3.19.0", {"start": v(-55.54, -88.88) * mm, "mid": v(-52.4, -90.76) * mm, "end": v(-49.2, -92.54) * mm});
            skLineSegment(sketch, "E34.4.19.0", {"start": v(-54.67, -102.82) * mm, "end": v(-49.2, -92.54) * mm});
            skArc(sketch, "E34.7.19.0", {"start": v(-61.71, -98.76) * mm, "mid": v(-58.23, -100.85) * mm, "end": v(-54.67, -102.82) * mm});
            skLineSegment(sketch, "E34.11.19.0", {"start": v(-55.54, -88.88) * mm, "end": v(-61.71, -98.76) * mm});
            skArc(sketch, "E34.3.20.0", {"start": v(-42.63, -95.74) * mm, "mid": v(-39.26, -97.17) * mm, "end": v(-35.84, -98.48) * mm});
            skLineSegment(sketch, "E34.4.20.0", {"start": v(-39.83, -109.43) * mm, "end": v(-35.84, -98.48) * mm});
            skArc(sketch, "E34.7.20.0", {"start": v(-47.37, -106.39) * mm, "mid": v(-43.63, -107.98) * mm, "end": v(-39.83, -109.43) * mm});
            skLineSegment(sketch, "E34.11.20.0", {"start": v(-42.63, -95.74) * mm, "end": v(-47.37, -106.39) * mm});
            skArc(sketch, "E34.3.21.0", {"start": v(-28.89, -100.74) * mm, "mid": v(-25.35, -101.69) * mm, "end": v(-21.79, -102.51) * mm});
            skLineSegment(sketch, "E34.4.21.0", {"start": v(-24.21, -113.91) * mm, "end": v(-21.79, -102.51) * mm});
            skArc(sketch, "E34.7.21.0", {"start": v(-32.1, -111.95) * mm, "mid": v(-28.17, -113) * mm, "end": v(-24.21, -113.91) * mm});
            skLineSegment(sketch, "E34.11.21.0", {"start": v(-28.89, -100.74) * mm, "end": v(-32.1, -111.95) * mm});
            skArc(sketch, "E34.3.22.0", {"start": v(-14.59, -103.78) * mm, "mid": v(-10.95, -104.23) * mm, "end": v(-7.31, -104.55) * mm});
            skLineSegment(sketch, "E34.4.22.0", {"start": v(-8.12, -116.17) * mm, "end": v(-7.31, -104.55) * mm});
            skArc(sketch, "E34.7.22.0", {"start": v(-16.2, -115.32) * mm, "mid": v(-12.17, -115.82) * mm, "end": v(-8.12, -116.17) * mm});
            skLineSegment(sketch, "E34.11.22.0", {"start": v(-14.59, -103.78) * mm, "end": v(-16.2, -115.32) * mm});
            skArc(sketch, "E34.3.23.0", {"start": v(0, -104.8) * mm, "mid": v(3.66, -104.74) * mm, "end": v(7.31, -104.55) * mm});
            skLineSegment(sketch, "E34.4.23.0", {"start": v(8.12, -116.17) * mm, "end": v(7.31, -104.55) * mm});
            skArc(sketch, "E34.7.23.0", {"start": v(0, -116.46) * mm, "mid": v(4.06, -116.39) * mm, "end": v(8.12, -116.17) * mm});
            skLineSegment(sketch, "E34.11.23.0", {"start": v(0, -104.8) * mm, "end": v(0, -116.46) * mm});
            skArc(sketch, "E34.3.24.0", {"start": v(14.59, -103.78) * mm, "mid": v(18.2, -103.21) * mm, "end": v(21.79, -102.51) * mm});
            skLineSegment(sketch, "E34.4.24.0", {"start": v(24.21, -113.91) * mm, "end": v(21.79, -102.51) * mm});
            skArc(sketch, "E34.7.24.0", {"start": v(16.2, -115.32) * mm, "mid": v(20.22, -114.69) * mm, "end": v(24.21, -113.91) * mm});
            skLineSegment(sketch, "E34.11.24.0", {"start": v(14.59, -103.78) * mm, "end": v(16.2, -115.32) * mm});
            skArc(sketch, "E34.3.25.0", {"start": v(28.89, -100.74) * mm, "mid": v(32.39, -99.67) * mm, "end": v(35.84, -98.48) * mm});
            skLineSegment(sketch, "E34.4.25.0", {"start": v(39.83, -109.43) * mm, "end": v(35.84, -98.48) * mm});
            skArc(sketch, "E34.7.25.0", {"start": v(32.1, -111.95) * mm, "mid": v(35.99, -110.76) * mm, "end": v(39.83, -109.43) * mm});
            skLineSegment(sketch, "E34.11.25.0", {"start": v(28.89, -100.74) * mm, "end": v(32.1, -111.95) * mm});
            skArc(sketch, "E34.3.26.0", {"start": v(42.63, -95.74) * mm, "mid": v(45.94, -94.2) * mm, "end": v(49.2, -92.54) * mm});
            skLineSegment(sketch, "E34.4.26.0", {"start": v(54.67, -102.82) * mm, "end": v(49.2, -92.54) * mm});
            skArc(sketch, "E34.7.26.0", {"start": v(47.37, -106.39) * mm, "mid": v(51.05, -104.67) * mm, "end": v(54.67, -102.82) * mm});
            skLineSegment(sketch, "E34.11.26.0", {"start": v(42.63, -95.74) * mm, "end": v(47.37, -106.39) * mm});
            skArc(sketch, "E34.3.27.0", {"start": v(55.54, -88.88) * mm, "mid": v(58.6, -86.89) * mm, "end": v(61.6, -84.79) * mm});
            skLineSegment(sketch, "E34.4.27.0", {"start": v(68.45, -94.22) * mm, "end": v(61.6, -84.79) * mm});
            skArc(sketch, "E34.7.27.0", {"start": v(61.71, -98.76) * mm, "mid": v(65.12, -96.55) * mm, "end": v(68.45, -94.22) * mm});
            skLineSegment(sketch, "E34.11.27.0", {"start": v(55.54, -88.88) * mm, "end": v(61.71, -98.76) * mm});
            skArc(sketch, "E34.3.28.0", {"start": v(67.37, -80.28) * mm, "mid": v(70.13, -77.88) * mm, "end": v(72.8, -75.39) * mm});
            skLineSegment(sketch, "E34.4.28.0", {"start": v(80.9, -83.77) * mm, "end": v(72.8, -75.39) * mm});
            skArc(sketch, "E34.7.28.0", {"start": v(74.86, -89.21) * mm, "mid": v(77.92, -86.54) * mm, "end": v(80.9, -83.77) * mm});
            skLineSegment(sketch, "E34.11.28.0", {"start": v(67.37, -80.28) * mm, "end": v(74.86, -89.21) * mm});
            skArc(sketch, "E34.3.29.0", {"start": v(77.88, -70.13) * mm, "mid": v(80.28, -67.37) * mm, "end": v(82.59, -64.52) * mm});
            skLineSegment(sketch, "E34.4.29.0", {"start": v(91.77, -71.7) * mm, "end": v(82.59, -64.52) * mm});
            skArc(sketch, "E34.7.29.0", {"start": v(86.54, -77.92) * mm, "mid": v(89.21, -74.86) * mm, "end": v(91.77, -71.7) * mm});
            skLineSegment(sketch, "E34.11.29.0", {"start": v(77.88, -70.13) * mm, "end": v(86.54, -77.92) * mm});
            skArc(sketch, "E34.3.30.0", {"start": v(86.89, -58.6) * mm, "mid": v(88.88, -55.54) * mm, "end": v(90.76, -52.4) * mm});
            skLineSegment(sketch, "E34.4.30.0", {"start": v(100.85, -58.23) * mm, "end": v(90.76, -52.4) * mm});
            skArc(sketch, "E34.7.30.0", {"start": v(96.55, -65.12) * mm, "mid": v(98.76, -61.71) * mm, "end": v(100.85, -58.23) * mm});
            skLineSegment(sketch, "E34.11.30.0", {"start": v(86.89, -58.6) * mm, "end": v(96.55, -65.12) * mm});
            skArc(sketch, "E34.3.31.0", {"start": v(94.2, -45.94) * mm, "mid": v(95.74, -42.63) * mm, "end": v(97.17, -39.26) * mm});
            skLineSegment(sketch, "E34.4.31.0", {"start": v(107.98, -43.63) * mm, "end": v(97.17, -39.26) * mm});
            skArc(sketch, "E34.7.31.0", {"start": v(104.67, -51.05) * mm, "mid": v(106.39, -47.37) * mm, "end": v(107.98, -43.63) * mm});
            skLineSegment(sketch, "E34.11.31.0", {"start": v(94.2, -45.94) * mm, "end": v(104.67, -51.05) * mm});
            skArc(sketch, "E34.3.32.0", {"start": v(99.67, -32.39) * mm, "mid": v(100.74, -28.89) * mm, "end": v(101.69, -25.35) * mm});
            skLineSegment(sketch, "E34.4.32.0", {"start": v(113, -28.17) * mm, "end": v(101.69, -25.35) * mm});
            skArc(sketch, "E34.7.32.0", {"start": v(110.76, -35.99) * mm, "mid": v(111.95, -32.1) * mm, "end": v(113, -28.17) * mm});
            skLineSegment(sketch, "E34.11.32.0", {"start": v(99.67, -32.39) * mm, "end": v(110.76, -35.99) * mm});
            skArc(sketch, "E34.3.33.0", {"start": v(103.21, -18.2) * mm, "mid": v(103.78, -14.59) * mm, "end": v(104.23, -10.95) * mm});
            skLineSegment(sketch, "E34.4.33.0", {"start": v(115.82, -12.17) * mm, "end": v(104.23, -10.95) * mm});
            skArc(sketch, "E34.7.33.0", {"start": v(114.69, -20.22) * mm, "mid": v(115.32, -16.2) * mm, "end": v(115.82, -12.17) * mm});
            skLineSegment(sketch, "E34.11.33.0", {"start": v(103.21, -18.2) * mm, "end": v(114.69, -20.22) * mm});
            skArc(sketch, "E34.3.34.0", {"start": v(104.74, -3.66) * mm, "mid": v(104.8, 0) * mm, "end": v(104.74, 3.66) * mm});
            skLineSegment(sketch, "E34.4.34.0", {"start": v(116.39, 4.06) * mm, "end": v(104.74, 3.66) * mm});
            skArc(sketch, "E34.7.34.0", {"start": v(116.39, -4.06) * mm, "mid": v(116.46, 0) * mm, "end": v(116.39, 4.06) * mm});
            skLineSegment(sketch, "E34.11.34.0", {"start": v(104.74, -3.66) * mm, "end": v(116.39, -4.06) * mm});
            skArc(sketch, "E34.3.35.0", {"start": v(104.23, 10.95) * mm, "mid": v(103.78, 14.59) * mm, "end": v(103.21, 18.2) * mm});
            skLineSegment(sketch, "E34.4.35.0", {"start": v(114.69, 20.22) * mm, "end": v(103.21, 18.2) * mm});
            skArc(sketch, "E34.7.35.0", {"start": v(115.82, 12.17) * mm, "mid": v(115.32, 16.2) * mm, "end": v(114.69, 20.22) * mm});
            skLineSegment(sketch, "E34.11.35.0", {"start": v(104.23, 10.95) * mm, "end": v(115.82, 12.17) * mm});
            skArc(sketch, "E35.3.36.0", {"start": v(101.69, 25.35) * mm, "mid": v(100.74, 28.89) * mm, "end": v(99.67, 32.39) * mm});
            skLineSegment(sketch, "E35.4.36.0", {"start": v(110.76, 35.99) * mm, "end": v(99.67, 32.39) * mm});
            skArc(sketch, "E35.7.36.0", {"start": v(113, 28.17) * mm, "mid": v(111.95, 32.1) * mm, "end": v(110.76, 35.99) * mm});
            skLineSegment(sketch, "E35.11.36.0", {"start": v(101.69, 25.35) * mm, "end": v(113, 28.17) * mm});
            skArc(sketch, "E35.3.37.0", {"start": v(97.17, 39.26) * mm, "mid": v(95.74, 42.63) * mm, "end": v(94.2, 45.94) * mm});
            skLineSegment(sketch, "E35.4.37.0", {"start": v(104.67, 51.05) * mm, "end": v(94.2, 45.94) * mm});
            skArc(sketch, "E35.7.37.0", {"start": v(107.98, 43.63) * mm, "mid": v(106.39, 47.37) * mm, "end": v(104.67, 51.05) * mm});
            skLineSegment(sketch, "E35.11.37.0", {"start": v(97.17, 39.26) * mm, "end": v(107.98, 43.63) * mm});
            skArc(sketch, "E35.3.38.0", {"start": v(90.76, 52.4) * mm, "mid": v(88.88, 55.54) * mm, "end": v(86.89, 58.6) * mm});
            skLineSegment(sketch, "E35.4.38.0", {"start": v(96.55, 65.12) * mm, "end": v(86.89, 58.6) * mm});
            skArc(sketch, "E35.7.38.0", {"start": v(100.85, 58.23) * mm, "mid": v(98.76, 61.71) * mm, "end": v(96.55, 65.12) * mm});
            skLineSegment(sketch, "E35.11.38.0", {"start": v(90.76, 52.4) * mm, "end": v(100.85, 58.23) * mm});
            skArc(sketch, "E35.3.39.0", {"start": v(82.59, 64.52) * mm, "mid": v(80.28, 67.37) * mm, "end": v(77.88, 70.13) * mm});
            skLineSegment(sketch, "E35.4.39.0", {"start": v(86.54, 77.92) * mm, "end": v(77.88, 70.13) * mm});
            skArc(sketch, "E35.7.39.0", {"start": v(91.77, 71.7) * mm, "mid": v(89.21, 74.86) * mm, "end": v(86.54, 77.92) * mm});
            skLineSegment(sketch, "E35.11.39.0", {"start": v(82.59, 64.52) * mm, "end": v(91.77, 71.7) * mm});
            skArc(sketch, "E35.3.40.0", {"start": v(72.8, 75.39) * mm, "mid": v(70.13, 77.88) * mm, "end": v(67.37, 80.28) * mm});
            skLineSegment(sketch, "E35.4.40.0", {"start": v(74.86, 89.21) * mm, "end": v(67.37, 80.28) * mm});
            skArc(sketch, "E35.7.40.0", {"start": v(80.9, 83.77) * mm, "mid": v(77.92, 86.54) * mm, "end": v(74.86, 89.21) * mm});
            skLineSegment(sketch, "E35.11.40.0", {"start": v(72.8, 75.39) * mm, "end": v(80.9, 83.77) * mm});
            skArc(sketch, "E35.3.41.0", {"start": v(61.6, 84.79) * mm, "mid": v(58.6, 86.89) * mm, "end": v(55.54, 88.88) * mm});
            skLineSegment(sketch, "E35.4.41.0", {"start": v(61.71, 98.76) * mm, "end": v(55.54, 88.88) * mm});
            skArc(sketch, "E35.7.41.0", {"start": v(68.45, 94.22) * mm, "mid": v(65.12, 96.55) * mm, "end": v(61.71, 98.76) * mm});
            skLineSegment(sketch, "E35.11.41.0", {"start": v(61.6, 84.79) * mm, "end": v(68.45, 94.22) * mm});
            skArc(sketch, "E35.3.42.0", {"start": v(49.2, 92.54) * mm, "mid": v(45.94, 94.2) * mm, "end": v(42.63, 95.74) * mm});
            skLineSegment(sketch, "E35.4.42.0", {"start": v(47.37, 106.39) * mm, "end": v(42.63, 95.74) * mm});
            skArc(sketch, "E35.7.42.0", {"start": v(54.67, 102.82) * mm, "mid": v(51.05, 104.67) * mm, "end": v(47.37, 106.39) * mm});
            skLineSegment(sketch, "E35.11.42.0", {"start": v(49.2, 92.54) * mm, "end": v(54.67, 102.82) * mm});
            skArc(sketch, "E35.3.43.0", {"start": v(35.84, 98.48) * mm, "mid": v(32.39, 99.67) * mm, "end": v(28.89, 100.74) * mm});
            skLineSegment(sketch, "E35.4.43.0", {"start": v(32.1, 111.95) * mm, "end": v(28.89, 100.74) * mm});
            skArc(sketch, "E35.7.43.0", {"start": v(39.83, 109.43) * mm, "mid": v(35.99, 110.76) * mm, "end": v(32.1, 111.95) * mm});
            skLineSegment(sketch, "E35.11.43.0", {"start": v(35.84, 98.48) * mm, "end": v(39.83, 109.43) * mm});
            skArc(sketch, "E35.3.44.0", {"start": v(21.79, 102.51) * mm, "mid": v(18.2, 103.21) * mm, "end": v(14.59, 103.78) * mm});
            skLineSegment(sketch, "E35.4.44.0", {"start": v(16.2, 115.32) * mm, "end": v(14.59, 103.78) * mm});
            skArc(sketch, "E35.7.44.0", {"start": v(24.21, 113.91) * mm, "mid": v(20.22, 114.69) * mm, "end": v(16.2, 115.32) * mm});
            skLineSegment(sketch, "E35.11.44.0", {"start": v(21.79, 102.51) * mm, "end": v(24.21, 113.91) * mm});
            skSolve(sketch);
        }
        {
            var Q0;
            Q0 = qSketchRegion(id + "F4", true);
            extrude(context, id + "F5", {"entities" : qUnion([Q0]), "operationType" : NewBodyOperationType.REMOVE, "oppositeDirection" : true, "depth" : 25 * mm, "offsetDistance" : 25 * mm});
        }
    });
